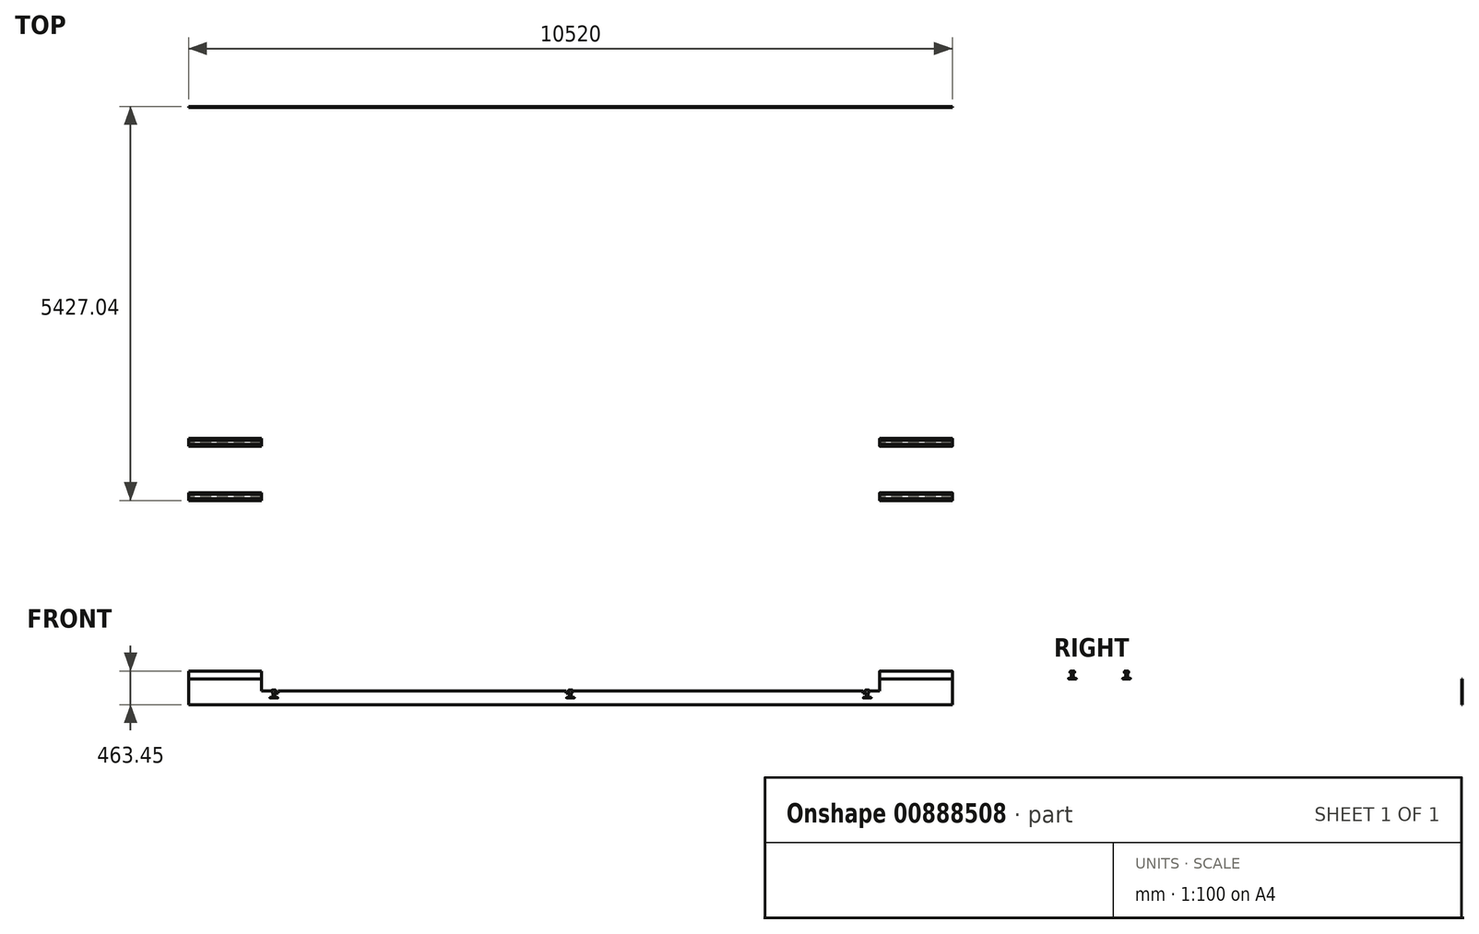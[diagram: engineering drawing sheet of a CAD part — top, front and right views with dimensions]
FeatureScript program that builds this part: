
annotation { "Feature Type Name" : "Feature", "Feature Type Description" : "" }
export const myFeature = defineFeature(function(context is Context, id is Id, definition is map)
    precondition{}
    {
        {
            var Q0;
            Q0=qCreatedBy(makeId("Front.planeOp"),FACE);
            var sketch = newSketch(context, id + "F0", { "sketchPlane" : qUnion([Q0])});
            skLineSegment(sketch, "E0", {"start": v(0, 0) * mm, "end": v(-4260, 0) * mm});
            skLineSegment(sketch, "E1", {"start": v(0, 0) * mm, "end": v(4260, 0) * mm});
            skLineSegment(sketch, "E2", {"start": v(-4260, 0) * mm, "end": v(-4260, 155.5) * mm});
            skLineSegment(sketch, "E3.MirrorCS", {"start": v(4260, 0) * mm, "end": v(4260, 155.5) * mm});
            skLineSegment(sketch, "E4", {"start": v(-4260, 155.5) * mm, "end": v(-5260, 155.5) * mm});
            skLineSegment(sketch, "E5.MirrorCS", {"start": v(4260, 155.5) * mm, "end": v(5260, 155.5) * mm});
            skLineSegment(sketch, "E6", {"start": v(-5260, 155.5) * mm, "end": v(-5260, -200) * mm});
            skLineSegment(sketch, "E7", {"start": v(-5260, -200) * mm, "end": v(0, -200) * mm});
            skLineSegment(sketch, "E8.MirrorCS", {"start": v(5260, -200) * mm, "end": v(0, -200) * mm});
            skLineSegment(sketch, "E9.MirrorCS", {"start": v(5260, 155.5) * mm, "end": v(5260, -200) * mm});
            skLineSegment(sketch, "E10", {"start": v(0, 0) * mm, "end": v(0, -1046.92) * mm, "construction": true});
            skLineSegment(sketch, "E11", {"start": v(-4087, 0) * mm, "end": v(-4087, -936.91) * mm, "construction": true});
            skLineSegment(sketch, "E12.MirrorCS", {"start": v(4087, 0) * mm, "end": v(4087, -936.91) * mm, "construction": true});
            skLineSegment(sketch, "E13", {"start": v(-4057, 0) * mm, "end": v(-4057, -40) * mm});
            skLineSegment(sketch, "E14", {"start": v(-4057, -40) * mm, "end": v(-4027, -40) * mm});
            skLineSegment(sketch, "E15", {"start": v(-4027, -40) * mm, "end": v(-4027, 0) * mm});
            skLineSegment(sketch, "E16.MirrorCS", {"start": v(4027, -40) * mm, "end": v(4027, 0) * mm});
            skLineSegment(sketch, "E17.MirrorCS", {"start": v(4057, -40) * mm, "end": v(4027, -40) * mm});
            skLineSegment(sketch, "E18.MirrorCS", {"start": v(4057, 0) * mm, "end": v(4057, -40) * mm});
            skLineSegment(sketch, "E19", {"start": v(-30, 0) * mm, "end": v(-30, -40) * mm});
            skLineSegment(sketch, "E20", {"start": v(-30, -40) * mm, "end": v(-60, -40) * mm});
            skLineSegment(sketch, "E21", {"start": v(-60, -40) * mm, "end": v(-60, 0) * mm});
            skLineSegment(sketch, "E22.0", {"start": v(0, -10) * mm, "end": v(-4260, -10) * mm});
            skLineSegment(sketch, "E23.MirrorCS", {"start": v(0, -10) * mm, "end": v(4260, -10) * mm});
            skLineSegment(sketch, "E24", {"start": v(-4260, 0) * mm, "end": v(-4260, -10) * mm});
            skLineSegment(sketch, "E25.MirrorCS", {"start": v(4260, 0) * mm, "end": v(4260, -10) * mm});
            skLineSegment(sketch, "E26", {"start": v(-4260, 155.5) * mm, "end": v(4260, 155.5) * mm});
            skLineSegment(sketch, "E27", {"start": v(-4260, 155.5) * mm, "end": v(-4260, 483.34) * mm});
            skLineSegment(sketch, "E28", {"start": v(-4260, 483.34) * mm, "end": v(4260, 483.34) * mm});
            skLineSegment(sketch, "E29", {"start": v(4260, 483.34) * mm, "end": v(4260, 155.5) * mm});
            skSolve(sketch);
        }
        {
            var Q0;
            Q0=qCreatedBy(makeId("Front.planeOp"),FACE);
            var sketch = newSketch(context, id + "F1", { "sketchPlane" : qUnion([Q0])});
            skLineSegment(sketch, "E30.MirrorCS", {"start": v(-30.17, -7.94) * mm, "end": v(-30.17, -22.72) * mm});
            skArc(sketch, "E31.MirrorCS", {"start": v(-30.17, -7.94) * mm, "mid": v(-27.84, -2.33) * mm, "end": v(-22.23, 0) * mm});
            skLineSegment(sketch, "E32.MirrorCS", {"start": v(0, 0) * mm, "end": v(-22.23, 0) * mm});
            skLineSegment(sketch, "E33.MirrorCS", {"start": v(0, 0) * mm, "end": v(22.22, 0) * mm});
            skArc(sketch, "E34.MirrorCS", {"start": v(30.16, -7.94) * mm, "mid": v(27.84, -2.33) * mm, "end": v(22.22, 0) * mm});
            skLineSegment(sketch, "E35.MirrorCS", {"start": v(30.16, -7.94) * mm, "end": v(30.16, -22.72) * mm});
            skArc(sketch, "E36.MirrorCS", {"start": v(28.93, -24.27) * mm, "mid": v(29.82, -23.71) * mm, "end": v(30.16, -22.72) * mm});
            skLineSegment(sketch, "E37.MirrorCS", {"start": v(17.22, -26.97) * mm, "end": v(28.93, -24.27) * mm});
            skArc(sketch, "E38.MirrorCS", {"start": v(17.22, -26.97) * mm, "mid": v(13.68, -29.2) * mm, "end": v(12.3, -33.16) * mm});
            skLineSegment(sketch, "E39.MirrorCS", {"start": v(12.3, -88.5) * mm, "end": v(12.3, -30.95) * mm});
            skArc(sketch, "E40.MirrorCS", {"start": v(12.3, -86.29) * mm, "mid": v(13.68, -90.24) * mm, "end": v(17.22, -92.48) * mm});
            skLineSegment(sketch, "E41.MirrorCS", {"start": v(17.22, -92.48) * mm, "end": v(52.74, -100.68) * mm});
            skArc(sketch, "E42.MirrorCS", {"start": v(53.97, -102.23) * mm, "mid": v(53.63, -101.24) * mm, "end": v(52.74, -100.68) * mm});
            skLineSegment(sketch, "E43.MirrorCS", {"start": v(53.97, -106.36) * mm, "end": v(53.97, -102.23) * mm});
            skArc(sketch, "E44.MirrorCS", {"start": v(52.38, -107.95) * mm, "mid": v(53.5, -107.48) * mm, "end": v(53.97, -106.36) * mm});
            skLineSegment(sketch, "E45.MirrorCS", {"start": v(-52.39, -107.95) * mm, "end": v(53.97, -107.95) * mm});
            skArc(sketch, "E46.MirrorCS", {"start": v(-52.39, -107.95) * mm, "mid": v(-53.5, -107.48) * mm, "end": v(-53.98, -106.36) * mm});
            skLineSegment(sketch, "E47.MirrorCS", {"start": v(-53.98, -106.36) * mm, "end": v(-53.98, -102.23) * mm});
            skArc(sketch, "E48.MirrorCS", {"start": v(-53.98, -102.23) * mm, "mid": v(-53.63, -101.24) * mm, "end": v(-52.74, -100.68) * mm});
            skLineSegment(sketch, "E49.MirrorCS", {"start": v(-17.22, -92.48) * mm, "end": v(-52.74, -100.68) * mm});
            skArc(sketch, "E50.MirrorCS", {"start": v(-12.3, -86.29) * mm, "mid": v(-13.68, -90.24) * mm, "end": v(-17.22, -92.48) * mm});
            skLineSegment(sketch, "E51.MirrorCS", {"start": v(-12.3, -86.29) * mm, "end": v(-12.3, -33.16) * mm});
            skArc(sketch, "E52.MirrorCS", {"start": v(-17.22, -26.97) * mm, "mid": v(-13.68, -29.2) * mm, "end": v(-12.3, -33.16) * mm});
            skLineSegment(sketch, "E53.MirrorCS", {"start": v(-17.22, -26.97) * mm, "end": v(-28.93, -24.27) * mm});
            skArc(sketch, "E54.MirrorCS", {"start": v(-28.93, -24.27) * mm, "mid": v(-29.82, -23.71) * mm, "end": v(-30.17, -22.72) * mm});
            skLineSegment(sketch, "E55.0", {"start": v(4087, 0) * mm, "end": v(4087, -936.91) * mm, "construction": true});
            skLineSegment(sketch, "E56.0", {"start": v(-4087, 0) * mm, "end": v(-4087, -936.91) * mm, "construction": true});
            skLineSegment(sketch, "E57.MirrorCS", {"start": v(4056.83, -7.94) * mm, "end": v(4056.83, -22.72) * mm});
            skArc(sketch, "E58.MirrorCS", {"start": v(4056.83, -7.94) * mm, "mid": v(4059.16, -2.33) * mm, "end": v(4064.77, 0) * mm});
            skLineSegment(sketch, "E59.MirrorCS", {"start": v(4087, 0) * mm, "end": v(4064.77, 0) * mm});
            skLineSegment(sketch, "E60.MirrorCS", {"start": v(4087, 0) * mm, "end": v(4109.22, 0) * mm});
            skArc(sketch, "E61.MirrorCS", {"start": v(4117.16, -7.94) * mm, "mid": v(4114.84, -2.33) * mm, "end": v(4109.22, 0) * mm});
            skLineSegment(sketch, "E62.MirrorCS", {"start": v(4117.16, -7.94) * mm, "end": v(4117.16, -22.72) * mm});
            skArc(sketch, "E63.MirrorCS", {"start": v(4115.93, -24.27) * mm, "mid": v(4116.82, -23.71) * mm, "end": v(4117.16, -22.72) * mm});
            skLineSegment(sketch, "E64.MirrorCS", {"start": v(4104.22, -26.97) * mm, "end": v(4115.93, -24.27) * mm});
            skArc(sketch, "E65.MirrorCS", {"start": v(4104.22, -26.97) * mm, "mid": v(4100.68, -29.2) * mm, "end": v(4099.3, -33.16) * mm});
            skLineSegment(sketch, "E66.MirrorCS", {"start": v(4099.3, -88.5) * mm, "end": v(4099.3, -30.95) * mm});
            skArc(sketch, "E67.MirrorCS", {"start": v(4099.3, -86.29) * mm, "mid": v(4100.68, -90.24) * mm, "end": v(4104.22, -92.48) * mm});
            skLineSegment(sketch, "E68.MirrorCS", {"start": v(4104.22, -92.48) * mm, "end": v(4139.74, -100.68) * mm});
            skArc(sketch, "E69.MirrorCS", {"start": v(4140.97, -102.23) * mm, "mid": v(4140.63, -101.24) * mm, "end": v(4139.74, -100.68) * mm});
            skLineSegment(sketch, "E70.MirrorCS", {"start": v(4140.97, -106.36) * mm, "end": v(4140.97, -102.23) * mm});
            skArc(sketch, "E71.MirrorCS", {"start": v(4139.38, -107.95) * mm, "mid": v(4140.5, -107.48) * mm, "end": v(4140.97, -106.36) * mm});
            skLineSegment(sketch, "E72.MirrorCS", {"start": v(4034.61, -107.95) * mm, "end": v(4140.97, -107.95) * mm});
            skArc(sketch, "E73.MirrorCS", {"start": v(4034.61, -107.95) * mm, "mid": v(4033.5, -107.48) * mm, "end": v(4033.02, -106.36) * mm});
            skLineSegment(sketch, "E74.MirrorCS", {"start": v(4033.02, -106.36) * mm, "end": v(4033.02, -102.23) * mm});
            skArc(sketch, "E75.MirrorCS", {"start": v(4033.02, -102.23) * mm, "mid": v(4033.37, -101.24) * mm, "end": v(4034.26, -100.68) * mm});
            skLineSegment(sketch, "E76.MirrorCS", {"start": v(4069.78, -92.48) * mm, "end": v(4034.26, -100.68) * mm});
            skArc(sketch, "E77.MirrorCS", {"start": v(4074.7, -86.29) * mm, "mid": v(4073.32, -90.24) * mm, "end": v(4069.78, -92.48) * mm});
            skLineSegment(sketch, "E78.MirrorCS", {"start": v(4074.7, -86.29) * mm, "end": v(4074.7, -33.16) * mm});
            skArc(sketch, "E79.MirrorCS", {"start": v(4069.78, -26.97) * mm, "mid": v(4073.32, -29.2) * mm, "end": v(4074.7, -33.16) * mm});
            skLineSegment(sketch, "E80.MirrorCS", {"start": v(4069.78, -26.97) * mm, "end": v(4058.07, -24.27) * mm});
            skArc(sketch, "E81.MirrorCS", {"start": v(4058.07, -24.27) * mm, "mid": v(4057.18, -23.71) * mm, "end": v(4056.83, -22.72) * mm});
            skLineSegment(sketch, "E82.MirrorCS", {"start": v(-4117.16, -7.94) * mm, "end": v(-4117.16, -22.72) * mm});
            skArc(sketch, "E83.MirrorCS", {"start": v(-4117.16, -7.94) * mm, "mid": v(-4114.84, -2.33) * mm, "end": v(-4109.23, 0) * mm});
            skLineSegment(sketch, "E84.MirrorCS", {"start": v(-4087, 0) * mm, "end": v(-4109.22, 0) * mm});
            skLineSegment(sketch, "E85.MirrorCS", {"start": v(-4087, 0) * mm, "end": v(-4064.78, 0) * mm});
            skArc(sketch, "E86.MirrorCS", {"start": v(-4056.84, -7.94) * mm, "mid": v(-4059.16, -2.33) * mm, "end": v(-4064.78, 0) * mm});
            skLineSegment(sketch, "E87.MirrorCS", {"start": v(-4056.84, -7.94) * mm, "end": v(-4056.84, -22.72) * mm});
            skArc(sketch, "E88.MirrorCS", {"start": v(-4058.07, -24.27) * mm, "mid": v(-4057.18, -23.71) * mm, "end": v(-4056.83, -22.72) * mm});
            skLineSegment(sketch, "E89.MirrorCS", {"start": v(-4069.78, -26.97) * mm, "end": v(-4058.07, -24.27) * mm});
            skArc(sketch, "E90.MirrorCS", {"start": v(-4069.78, -26.97) * mm, "mid": v(-4073.32, -29.2) * mm, "end": v(-4074.7, -33.16) * mm});
            skLineSegment(sketch, "E91.MirrorCS", {"start": v(-4074.7, -88.5) * mm, "end": v(-4074.7, -30.95) * mm});
            skArc(sketch, "E92.MirrorCS", {"start": v(-4074.7, -86.29) * mm, "mid": v(-4073.32, -90.24) * mm, "end": v(-4069.78, -92.48) * mm});
            skLineSegment(sketch, "E93.MirrorCS", {"start": v(-4069.78, -92.48) * mm, "end": v(-4034.26, -100.68) * mm});
            skArc(sketch, "E94.MirrorCS", {"start": v(-4033.03, -102.23) * mm, "mid": v(-4033.37, -101.24) * mm, "end": v(-4034.26, -100.68) * mm});
            skLineSegment(sketch, "E95.MirrorCS", {"start": v(-4033.03, -106.36) * mm, "end": v(-4033.03, -102.23) * mm});
            skArc(sketch, "E96.MirrorCS", {"start": v(-4034.62, -107.95) * mm, "mid": v(-4033.5, -107.48) * mm, "end": v(-4033.03, -106.36) * mm});
            skLineSegment(sketch, "E97.MirrorCS", {"start": v(-4139.39, -107.95) * mm, "end": v(-4033.03, -107.95) * mm});
            skArc(sketch, "E98.MirrorCS", {"start": v(-4139.39, -107.95) * mm, "mid": v(-4140.5, -107.48) * mm, "end": v(-4140.98, -106.36) * mm});
            skLineSegment(sketch, "E99.MirrorCS", {"start": v(-4140.98, -106.36) * mm, "end": v(-4140.98, -102.23) * mm});
            skArc(sketch, "E100.MirrorCS", {"start": v(-4140.98, -102.23) * mm, "mid": v(-4140.63, -101.24) * mm, "end": v(-4139.74, -100.68) * mm});
            skLineSegment(sketch, "E101.MirrorCS", {"start": v(-4104.22, -92.48) * mm, "end": v(-4139.74, -100.68) * mm});
            skArc(sketch, "E102.MirrorCS", {"start": v(-4099.3, -86.29) * mm, "mid": v(-4100.68, -90.24) * mm, "end": v(-4104.22, -92.48) * mm});
            skLineSegment(sketch, "E103.MirrorCS", {"start": v(-4099.3, -86.29) * mm, "end": v(-4099.3, -33.16) * mm});
            skArc(sketch, "E104.MirrorCS", {"start": v(-4104.22, -26.97) * mm, "mid": v(-4100.68, -29.2) * mm, "end": v(-4099.3, -33.16) * mm});
            skLineSegment(sketch, "E105.MirrorCS", {"start": v(-4104.22, -26.97) * mm, "end": v(-4115.93, -24.27) * mm});
            skArc(sketch, "E106.MirrorCS", {"start": v(-4115.93, -24.27) * mm, "mid": v(-4116.82, -23.71) * mm, "end": v(-4117.16, -22.72) * mm});
            skSolve(sketch);
        }
        {
            assignVariable(context, id + "F2", {"name" : "a", "anyValue" : 10});
        }
        {
            var Q0;
            Q0=makeQuery(id+"F0.imprint","IMPRINT",FACE,{"disambiguationData":[TD([[makeQuery(id+"F0.imprint","IMPRINT",EDGE,{"derivedFrom":sQuery(id+"F0.wireOp",EDGE,"E2")}),1.0]])]});
            extrude(context, id + "F3", {"entities" : qUnion([Q0]), "depth" : (getVariable(context, 'a')) * mm, "offsetDistance" : 25 * mm});
        }
        {
            var Q0;
            Q0=makeQuery(id+"F1.imprint","IMPRINT",FACE,{"disambiguationData":[TD([[makeQuery(id+"F1.imprint","IMPRINT",EDGE,{"derivedFrom":sQuery(id+"F1.wireOp",EDGE,"E30.MirrorCS")}),1.0]])]});
            var Q1;
            Q1=makeQuery(id+"F1.imprint","IMPRINT",FACE,{"disambiguationData":[TD([[makeQuery(id+"F1.imprint","IMPRINT",EDGE,{"derivedFrom":sQuery(id+"F1.wireOp",EDGE,"E82.MirrorCS")}),1.0]])]});
            var Q2;
            Q2=makeQuery(id+"F1.imprint","IMPRINT",FACE,{"disambiguationData":[TD([[makeQuery(id+"F1.imprint","IMPRINT",EDGE,{"derivedFrom":sQuery(id+"F1.wireOp",EDGE,"E57.MirrorCS")}),1.0]])]});
            extrude(context, id + "F4", {"entities" : qUnion([Q0, Q1, Q2]), "operationType" : NewBodyOperationType.REMOVE, "depth" : (getVariable(context, 'a')) * mm, "offsetDistance" : 25 * mm});
        }
        {
            var Q0;
            Q0=makeQuery(id+"F1.imprint","IMPRINT",FACE,{"disambiguationData":[TD([[makeQuery(id+"F1.imprint","IMPRINT",EDGE,{"derivedFrom":sQuery(id+"F1.wireOp",EDGE,"E30.MirrorCS")}),1.0]])]});
            var Q1;
            Q1=makeQuery(id+"F1.imprint","IMPRINT",FACE,{"disambiguationData":[TD([[makeQuery(id+"F1.imprint","IMPRINT",EDGE,{"derivedFrom":sQuery(id+"F1.wireOp",EDGE,"E82.MirrorCS")}),1.0]])]});
            var Q2;
            Q2=makeQuery(id+"F1.imprint","IMPRINT",FACE,{"disambiguationData":[TD([[makeQuery(id+"F1.imprint","IMPRINT",EDGE,{"derivedFrom":sQuery(id+"F1.wireOp",EDGE,"E57.MirrorCS")}),1.0]])]});
            extrude(context, id + "F5", {"entities" : qUnion([Q0, Q1, Q2]), "depth" : (getVariable(context, 'a')) * mm, "offsetDistance" : 25 * mm});
        }
        {
            var Q0;
            Q0=makeQuery(id+"F3.opExtrude","SWEPT_FACE",FACE,{"disambiguationData":[OSD([sQuery(id+"F0.wireOp",EDGE,"E6")])]});
            var sketch = newSketch(context, id + "F6", { "sketchPlane" : qUnion([Q0])});
            skLineSegment(sketch, "E107", {"start": v(5000, 155.5) * mm, "end": v(5000, -200) * mm, "construction": true});
            skLineSegment(sketch, "E108.0", {"start": v(4314.2, 153.5) * mm, "end": v(4314.2, -200) * mm, "construction": true});
            skLineSegment(sketch, "E109.0", {"start": v(5685.8, 153.5) * mm, "end": v(5685.8, -200) * mm, "construction": true});
            skLineSegment(sketch, "E110.0", {"start": v(10000, 155.5) * mm, "end": v(0, 155.5) * mm});
            skLineSegment(sketch, "E111.0", {"start": v(10000, 145.5) * mm, "end": v(0, 145.5) * mm});
            skLineSegment(sketch, "E112.MirrorCS", {"start": v(4253.87, 145.56) * mm, "end": v(4253.87, 130.78) * mm});
            skArc(sketch, "E113.MirrorCS", {"start": v(4253.87, 145.56) * mm, "mid": v(4256.2, 151.17) * mm, "end": v(4261.8, 153.5) * mm});
            skLineSegment(sketch, "E114.MirrorCS", {"start": v(4284.03, 153.5) * mm, "end": v(4261.81, 153.5) * mm});
            skLineSegment(sketch, "E115.MirrorCS", {"start": v(4284.03, 153.5) * mm, "end": v(4306.26, 153.5) * mm});
            skArc(sketch, "E116.MirrorCS", {"start": v(4314.2, 145.56) * mm, "mid": v(4311.87, 151.17) * mm, "end": v(4306.26, 153.5) * mm});
            skLineSegment(sketch, "E117.MirrorCS", {"start": v(4314.2, 145.56) * mm, "end": v(4314.2, 130.78) * mm});
            skArc(sketch, "E118.MirrorCS", {"start": v(4312.97, 129.23) * mm, "mid": v(4313.85, 129.79) * mm, "end": v(4314.2, 130.78) * mm});
            skLineSegment(sketch, "E119.MirrorCS", {"start": v(4301.26, 126.53) * mm, "end": v(4312.97, 129.23) * mm});
            skArc(sketch, "E120.MirrorCS", {"start": v(4301.26, 126.53) * mm, "mid": v(4297.72, 124.3) * mm, "end": v(4296.34, 120.34) * mm});
            skLineSegment(sketch, "E121.MirrorCS", {"start": v(4296.34, 65) * mm, "end": v(4296.34, 122.55) * mm});
            skArc(sketch, "E122.MirrorCS", {"start": v(4296.34, 67.21) * mm, "mid": v(4297.72, 63.26) * mm, "end": v(4301.26, 61.02) * mm});
            skLineSegment(sketch, "E123.MirrorCS", {"start": v(4301.26, 61.02) * mm, "end": v(4336.78, 52.82) * mm});
            skArc(sketch, "E124.MirrorCS", {"start": v(4338, 51.27) * mm, "mid": v(4337.66, 52.26) * mm, "end": v(4336.78, 52.82) * mm});
            skLineSegment(sketch, "E125.MirrorCS", {"start": v(4338, 47.14) * mm, "end": v(4338, 51.27) * mm});
            skArc(sketch, "E126.MirrorCS", {"start": v(4336.42, 45.55) * mm, "mid": v(4337.54, 46.02) * mm, "end": v(4338, 47.14) * mm});
            skLineSegment(sketch, "E127.MirrorCS", {"start": v(4231.65, 45.55) * mm, "end": v(4338, 45.55) * mm});
            skArc(sketch, "E128.MirrorCS", {"start": v(4231.65, 45.55) * mm, "mid": v(4230.53, 46.02) * mm, "end": v(4230.06, 47.14) * mm});
            skLineSegment(sketch, "E129.MirrorCS", {"start": v(4230.06, 47.14) * mm, "end": v(4230.06, 51.27) * mm});
            skArc(sketch, "E130.MirrorCS", {"start": v(4230.06, 51.27) * mm, "mid": v(4230.4, 52.26) * mm, "end": v(4231.3, 52.82) * mm});
            skLineSegment(sketch, "E131.MirrorCS", {"start": v(4266.81, 61.02) * mm, "end": v(4231.3, 52.82) * mm});
            skArc(sketch, "E132.MirrorCS", {"start": v(4271.74, 67.21) * mm, "mid": v(4270.35, 63.26) * mm, "end": v(4266.81, 61.02) * mm});
            skLineSegment(sketch, "E133.MirrorCS", {"start": v(4271.73, 67.21) * mm, "end": v(4271.73, 120.34) * mm});
            skArc(sketch, "E134.MirrorCS", {"start": v(4266.81, 126.53) * mm, "mid": v(4270.35, 124.3) * mm, "end": v(4271.74, 120.34) * mm});
            skLineSegment(sketch, "E135.MirrorCS", {"start": v(4266.81, 126.53) * mm, "end": v(4255.1, 129.23) * mm});
            skArc(sketch, "E136.MirrorCS", {"start": v(4255.1, 129.23) * mm, "mid": v(4254.22, 129.79) * mm, "end": v(4253.87, 130.78) * mm});
            skLineSegment(sketch, "E137.MirrorCS", {"start": v(5685.8, 118.78) * mm, "end": v(5685.8, 104) * mm});
            skArc(sketch, "E138.MirrorCS", {"start": v(5685.8, 145.56) * mm, "mid": v(5688.13, 151.17) * mm, "end": v(5693.74, 153.5) * mm});
            skLineSegment(sketch, "E139.MirrorCS", {"start": v(5715.97, 153.5) * mm, "end": v(5693.74, 153.5) * mm});
            skLineSegment(sketch, "E140.MirrorCS", {"start": v(5715.97, 153.5) * mm, "end": v(5738.2, 153.5) * mm});
            skArc(sketch, "E141.MirrorCS", {"start": v(5746.13, 145.56) * mm, "mid": v(5743.8, 151.17) * mm, "end": v(5738.2, 153.5) * mm});
            skLineSegment(sketch, "E142.MirrorCS", {"start": v(5746.13, 145.56) * mm, "end": v(5746.13, 130.78) * mm});
            skArc(sketch, "E143.MirrorCS", {"start": v(5744.9, 129.23) * mm, "mid": v(5745.78, 129.79) * mm, "end": v(5746.13, 130.78) * mm});
            skLineSegment(sketch, "E144.MirrorCS", {"start": v(5733.19, 126.53) * mm, "end": v(5744.9, 129.23) * mm});
            skArc(sketch, "E145.MirrorCS", {"start": v(5733.19, 126.53) * mm, "mid": v(5729.65, 124.3) * mm, "end": v(5728.27, 120.34) * mm});
            skLineSegment(sketch, "E146.MirrorCS", {"start": v(5728.27, 65) * mm, "end": v(5728.27, 122.55) * mm});
            skArc(sketch, "E147.MirrorCS", {"start": v(5728.27, 67.21) * mm, "mid": v(5729.65, 63.26) * mm, "end": v(5733.19, 61.02) * mm});
            skLineSegment(sketch, "E148.MirrorCS", {"start": v(5733.19, 61.02) * mm, "end": v(5768.7, 52.82) * mm});
            skArc(sketch, "E149.MirrorCS", {"start": v(5769.94, 51.27) * mm, "mid": v(5769.6, 52.26) * mm, "end": v(5768.7, 52.82) * mm});
            skLineSegment(sketch, "E150.MirrorCS", {"start": v(5769.94, 47.14) * mm, "end": v(5769.94, 51.27) * mm});
            skArc(sketch, "E151.MirrorCS", {"start": v(5768.35, 45.55) * mm, "mid": v(5769.47, 46.02) * mm, "end": v(5769.94, 47.14) * mm});
            skLineSegment(sketch, "E152.MirrorCS", {"start": v(5663.58, 45.55) * mm, "end": v(5769.94, 45.55) * mm});
            skArc(sketch, "E153.MirrorCS", {"start": v(5663.58, 45.55) * mm, "mid": v(5662.46, 46.02) * mm, "end": v(5662, 47.14) * mm});
            skLineSegment(sketch, "E154.MirrorCS", {"start": v(5662, 47.14) * mm, "end": v(5662, 51.27) * mm});
            skArc(sketch, "E155.MirrorCS", {"start": v(5662, 51.27) * mm, "mid": v(5662.34, 52.26) * mm, "end": v(5663.22, 52.82) * mm});
            skLineSegment(sketch, "E156.MirrorCS", {"start": v(5698.74, 61.02) * mm, "end": v(5663.22, 52.82) * mm});
            skArc(sketch, "E157.MirrorCS", {"start": v(5703.67, 67.21) * mm, "mid": v(5702.28, 63.26) * mm, "end": v(5698.74, 61.02) * mm});
            skLineSegment(sketch, "E158.MirrorCS", {"start": v(5703.66, 67.21) * mm, "end": v(5703.66, 120.34) * mm});
            skArc(sketch, "E159.MirrorCS", {"start": v(5698.74, 126.53) * mm, "mid": v(5702.28, 124.3) * mm, "end": v(5703.67, 120.34) * mm});
            skLineSegment(sketch, "E160.MirrorCS", {"start": v(5698.74, 126.53) * mm, "end": v(5687.03, 129.23) * mm});
            skArc(sketch, "E161.MirrorCS", {"start": v(5687.03, 129.23) * mm, "mid": v(5686.15, 129.79) * mm, "end": v(5685.8, 130.78) * mm});
            skLineSegment(sketch, "E162", {"start": v(5685.8, 153.5) * mm, "end": v(5685.8, 113.5) * mm});
            skLineSegment(sketch, "E163", {"start": v(4314.2, 113.5) * mm, "end": v(4314.2, 153.5) * mm});
            skLineSegment(sketch, "E164", {"start": v(5746.13, 145.5) * mm, "end": v(5746.13, 155.5) * mm});
            skLineSegment(sketch, "E165.MirrorCS", {"start": v(4253.87, 145.5) * mm, "end": v(4253.87, 155.5) * mm});
            skLineSegment(sketch, "E166.MirrorCS", {"start": v(5687.39, 155.5) * mm, "end": v(5793.75, 155.5) * mm});
            skLineSegment(sketch, "E167.MirrorCS", {"start": v(4207.84, 155.5) * mm, "end": v(4314.2, 155.5) * mm});
            skLineSegment(sketch, "E168", {"start": v(5000, 155.5) * mm, "end": v(5000, 322.83) * mm, "construction": true});
            skLineSegment(sketch, "E169", {"start": v(5000, 247.79) * mm, "end": v(5342.9, 247.79) * mm, "construction": true});
            skLineSegment(sketch, "E170", {"start": v(5000, 247.79) * mm, "end": v(4657.1, 247.79) * mm, "construction": true});
            skLineSegment(sketch, "E171", {"start": v(4657.1, 247.79) * mm, "end": v(4657.1, 103.64) * mm, "construction": true});
            skLineSegment(sketch, "E172", {"start": v(5342.9, 247.79) * mm, "end": v(5342.9, 109.13) * mm, "construction": true});
            skLineSegment(sketch, "E173.MirrorCS", {"start": v(5342.9, 255.51) * mm, "end": v(5342.9, 240.73) * mm});
            skArc(sketch, "E174.MirrorCS", {"start": v(5342.9, 255.51) * mm, "mid": v(5345.23, 261.12) * mm, "end": v(5350.84, 263.45) * mm});
            skLineSegment(sketch, "E175.MirrorCS", {"start": v(5373.07, 263.45) * mm, "end": v(5350.84, 263.45) * mm});
            skLineSegment(sketch, "E176.MirrorCS", {"start": v(5373.07, 263.45) * mm, "end": v(5395.29, 263.45) * mm});
            skArc(sketch, "E177.MirrorCS", {"start": v(5403.23, 255.51) * mm, "mid": v(5400.9, 261.12) * mm, "end": v(5395.29, 263.45) * mm});
            skLineSegment(sketch, "E178.MirrorCS", {"start": v(5403.23, 255.51) * mm, "end": v(5403.23, 240.73) * mm});
            skArc(sketch, "E179.MirrorCS", {"start": v(5402, 239.18) * mm, "mid": v(5402.88, 239.74) * mm, "end": v(5403.23, 240.73) * mm});
            skLineSegment(sketch, "E180.MirrorCS", {"start": v(5390.29, 236.48) * mm, "end": v(5402, 239.18) * mm});
            skArc(sketch, "E181.MirrorCS", {"start": v(5390.29, 236.48) * mm, "mid": v(5386.75, 234.24) * mm, "end": v(5385.36, 230.29) * mm});
            skLineSegment(sketch, "E182.MirrorCS", {"start": v(5385.36, 174.95) * mm, "end": v(5385.36, 232.5) * mm});
            skArc(sketch, "E183.MirrorCS", {"start": v(5385.36, 177.16) * mm, "mid": v(5386.75, 173.2) * mm, "end": v(5390.29, 170.97) * mm});
            skLineSegment(sketch, "E184.MirrorCS", {"start": v(5390.29, 170.97) * mm, "end": v(5425.8, 162.77) * mm});
            skArc(sketch, "E185.MirrorCS", {"start": v(5427.04, 161.22) * mm, "mid": v(5426.7, 162.21) * mm, "end": v(5425.8, 162.77) * mm});
            skLineSegment(sketch, "E186.MirrorCS", {"start": v(5427.04, 157.1) * mm, "end": v(5427.04, 161.22) * mm});
            skArc(sketch, "E187.MirrorCS", {"start": v(5425.45, 155.5) * mm, "mid": v(5426.57, 155.97) * mm, "end": v(5427.04, 157.1) * mm});
            skLineSegment(sketch, "E188.MirrorCS", {"start": v(5320.68, 155.5) * mm, "end": v(5427.04, 155.5) * mm});
            skArc(sketch, "E189.MirrorCS", {"start": v(5320.68, 155.5) * mm, "mid": v(5319.56, 155.97) * mm, "end": v(5319.09, 157.1) * mm});
            skLineSegment(sketch, "E190.MirrorCS", {"start": v(5319.09, 157.1) * mm, "end": v(5319.09, 161.22) * mm});
            skArc(sketch, "E191.MirrorCS", {"start": v(5319.09, 161.22) * mm, "mid": v(5319.44, 162.21) * mm, "end": v(5320.32, 162.77) * mm});
            skLineSegment(sketch, "E192.MirrorCS", {"start": v(5355.84, 170.97) * mm, "end": v(5320.32, 162.77) * mm});
            skArc(sketch, "E193.MirrorCS", {"start": v(5360.77, 177.16) * mm, "mid": v(5359.38, 173.2) * mm, "end": v(5355.84, 170.97) * mm});
            skLineSegment(sketch, "E194.MirrorCS", {"start": v(5360.76, 177.16) * mm, "end": v(5360.76, 230.29) * mm});
            skArc(sketch, "E195.MirrorCS", {"start": v(5355.84, 236.48) * mm, "mid": v(5359.38, 234.24) * mm, "end": v(5360.77, 230.29) * mm});
            skLineSegment(sketch, "E196.MirrorCS", {"start": v(5355.84, 236.48) * mm, "end": v(5344.13, 239.18) * mm});
            skArc(sketch, "E197.MirrorCS", {"start": v(5344.13, 239.18) * mm, "mid": v(5343.25, 239.74) * mm, "end": v(5342.9, 240.73) * mm});
            skLineSegment(sketch, "E198.MirrorCS", {"start": v(4596.77, 255.51) * mm, "end": v(4596.77, 240.73) * mm});
            skArc(sketch, "E199.MirrorCS", {"start": v(4596.77, 255.51) * mm, "mid": v(4599.1, 261.12) * mm, "end": v(4604.71, 263.45) * mm});
            skLineSegment(sketch, "E200.MirrorCS", {"start": v(4626.94, 263.45) * mm, "end": v(4604.71, 263.45) * mm});
            skLineSegment(sketch, "E201.MirrorCS", {"start": v(4626.94, 263.45) * mm, "end": v(4649.16, 263.45) * mm});
            skArc(sketch, "E202.MirrorCS", {"start": v(4657.1, 255.51) * mm, "mid": v(4654.77, 261.12) * mm, "end": v(4649.16, 263.45) * mm});
            skLineSegment(sketch, "E203.MirrorCS", {"start": v(4657.1, 255.51) * mm, "end": v(4657.1, 240.73) * mm});
            skArc(sketch, "E204.MirrorCS", {"start": v(4655.87, 239.18) * mm, "mid": v(4656.75, 239.74) * mm, "end": v(4657.1, 240.73) * mm});
            skLineSegment(sketch, "E205.MirrorCS", {"start": v(4644.16, 236.48) * mm, "end": v(4655.87, 239.18) * mm});
            skArc(sketch, "E206.MirrorCS", {"start": v(4644.16, 236.48) * mm, "mid": v(4640.62, 234.24) * mm, "end": v(4639.24, 230.29) * mm});
            skLineSegment(sketch, "E207.MirrorCS", {"start": v(4639.24, 174.95) * mm, "end": v(4639.24, 232.5) * mm});
            skArc(sketch, "E208.MirrorCS", {"start": v(4639.24, 177.16) * mm, "mid": v(4640.62, 173.2) * mm, "end": v(4644.16, 170.97) * mm});
            skLineSegment(sketch, "E209.MirrorCS", {"start": v(4644.16, 170.97) * mm, "end": v(4679.68, 162.77) * mm});
            skArc(sketch, "E210.MirrorCS", {"start": v(4680.91, 161.22) * mm, "mid": v(4680.56, 162.21) * mm, "end": v(4679.68, 162.77) * mm});
            skLineSegment(sketch, "E211.MirrorCS", {"start": v(4680.91, 157.1) * mm, "end": v(4680.91, 161.22) * mm});
            skArc(sketch, "E212.MirrorCS", {"start": v(4679.32, 155.5) * mm, "mid": v(4680.44, 155.97) * mm, "end": v(4680.91, 157.1) * mm});
            skLineSegment(sketch, "E213.MirrorCS", {"start": v(4574.55, 155.5) * mm, "end": v(4680.91, 155.5) * mm});
            skArc(sketch, "E214.MirrorCS", {"start": v(4574.55, 155.5) * mm, "mid": v(4573.43, 155.97) * mm, "end": v(4572.96, 157.1) * mm});
            skLineSegment(sketch, "E215.MirrorCS", {"start": v(4572.96, 157.1) * mm, "end": v(4572.96, 161.22) * mm});
            skArc(sketch, "E216.MirrorCS", {"start": v(4572.96, 161.22) * mm, "mid": v(4573.3, 162.21) * mm, "end": v(4574.2, 162.77) * mm});
            skLineSegment(sketch, "E217.MirrorCS", {"start": v(4609.71, 170.97) * mm, "end": v(4574.2, 162.77) * mm});
            skArc(sketch, "E218.MirrorCS", {"start": v(4614.64, 177.16) * mm, "mid": v(4613.25, 173.2) * mm, "end": v(4609.71, 170.97) * mm});
            skLineSegment(sketch, "E219.MirrorCS", {"start": v(4614.64, 177.16) * mm, "end": v(4614.64, 230.29) * mm});
            skArc(sketch, "E220.MirrorCS", {"start": v(4609.71, 236.48) * mm, "mid": v(4613.25, 234.24) * mm, "end": v(4614.64, 230.29) * mm});
            skLineSegment(sketch, "E221.MirrorCS", {"start": v(4609.71, 236.48) * mm, "end": v(4598, 239.18) * mm});
            skArc(sketch, "E222.MirrorCS", {"start": v(4598, 239.18) * mm, "mid": v(4597.12, 239.74) * mm, "end": v(4596.77, 240.73) * mm});
            skSolve(sketch);
        }
        {
            var Q0;
            Q0=makeQuery(id+"F6.imprint","IMPRINT",FACE,{"disambiguationData":[TD([[makeQuery(id+"F6.imprint","IMPRINT",EDGE,{"derivedFrom":sQuery(id+"F6.wireOp",EDGE,"E198.MirrorCS")}),1.0]])]});
            var Q1;
            Q1=makeQuery(id+"F6.imprint","IMPRINT",FACE,{"disambiguationData":[TD([[makeQuery(id+"F6.imprint","IMPRINT",EDGE,{"derivedFrom":sQuery(id+"F6.wireOp",EDGE,"E173.MirrorCS")}),1.0]])]});
            var Q2;
            Q2=makeQuery(id+"F3.opExtrude","SWEPT_FACE",FACE,{"disambiguationData":[OSD([sQuery(id+"F0.wireOp",EDGE,"E9.MirrorCS")])]});
            extrude(context, id + "F7", {"entities" : qUnion([Q0, Q1]), "endBound" : BoundingType.UP_TO_SURFACE, "oppositeDirection" : true, "depth" : 25 * mm, "endBoundEntityFace" : qUnion([Q2]), "offsetDistance" : 25 * mm});
        }
        {
            var Q0;
            Q0=makeQuery(id+"F0.imprint","IMPRINT",FACE,{"disambiguationData":[TD([[makeQuery(id+"F0.imprint","IMPRINT",EDGE,{"derivedFrom":sQuery(id+"F0.wireOp",EDGE,"E26")}),1.0]])]});
            var Q1;
            {var subQ1=sQuery(id+"F0.wireOp",EDGE,"E2");Q1=makeQuery(id+"F0.imprint","IMPRINT",FACE,{"disambiguationData":[TD([[makeQuery(id+"F0.imprint","IMPRINT",EDGE,{"derivedFrom":subQ1}),-1.0]])]});}
            extrude(context, id + "F8", {"entities" : qUnion([Q0, Q1]), "operationType" : NewBodyOperationType.REMOVE, "endBound" : BoundingType.THROUGH_ALL, "depth" : 25 * mm, "offsetDistance" : 25 * mm});
        }
    });
